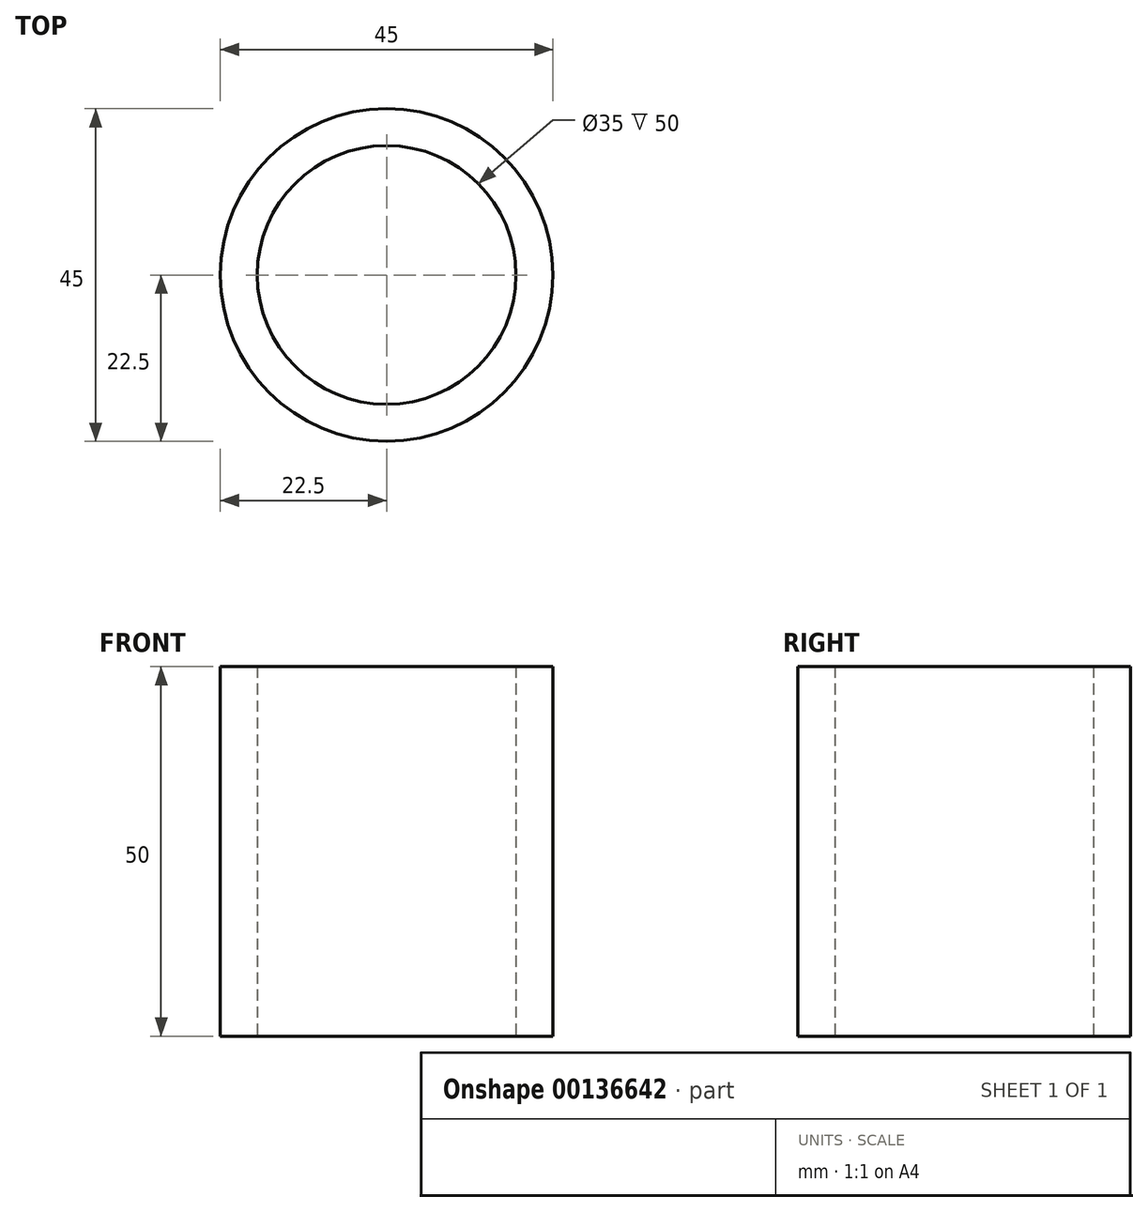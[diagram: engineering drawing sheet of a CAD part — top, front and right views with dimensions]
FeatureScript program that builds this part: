
annotation { "Feature Type Name" : "Feature", "Feature Type Description" : "" }
export const myFeature = defineFeature(function(context is Context, id is Id, definition is map)
    precondition{}
    {
        {
            assignVariable(context, id + "F0", {"name" : "shaft_h", "anyValue" : 50});
        }
        {
            var Q0;
            Q0=qCreatedBy(makeId("Top.planeOp"),FACE);
            var sketch = newSketch(context, id + "F1", { "sketchPlane" : qUnion([Q0])});
            skCircle(sketch, "E0", {"center": v(0, 0) * mm, "radius": 22.5 * mm});
            skCircle(sketch, "E1", {"center": v(0, 0) * mm, "radius": 17.5 * mm});
            skSolve(sketch);
        }
        {
            var Q0;
            Q0=makeQuery(id+"F1.imprint","IMPRINT",FACE,{"disambiguationData":[TD([[makeQuery(id+"F1.imprint","IMPRINT",EDGE,{"derivedFrom":sQuery(id+"F1.wireOp",EDGE,"E0")}),1.0]])]});
            extrude(context, id + "F2", {"entities" : qUnion([Q0]), "depth" : (getVariable(context, 'shaft_h')) * mm});
        }
    });
